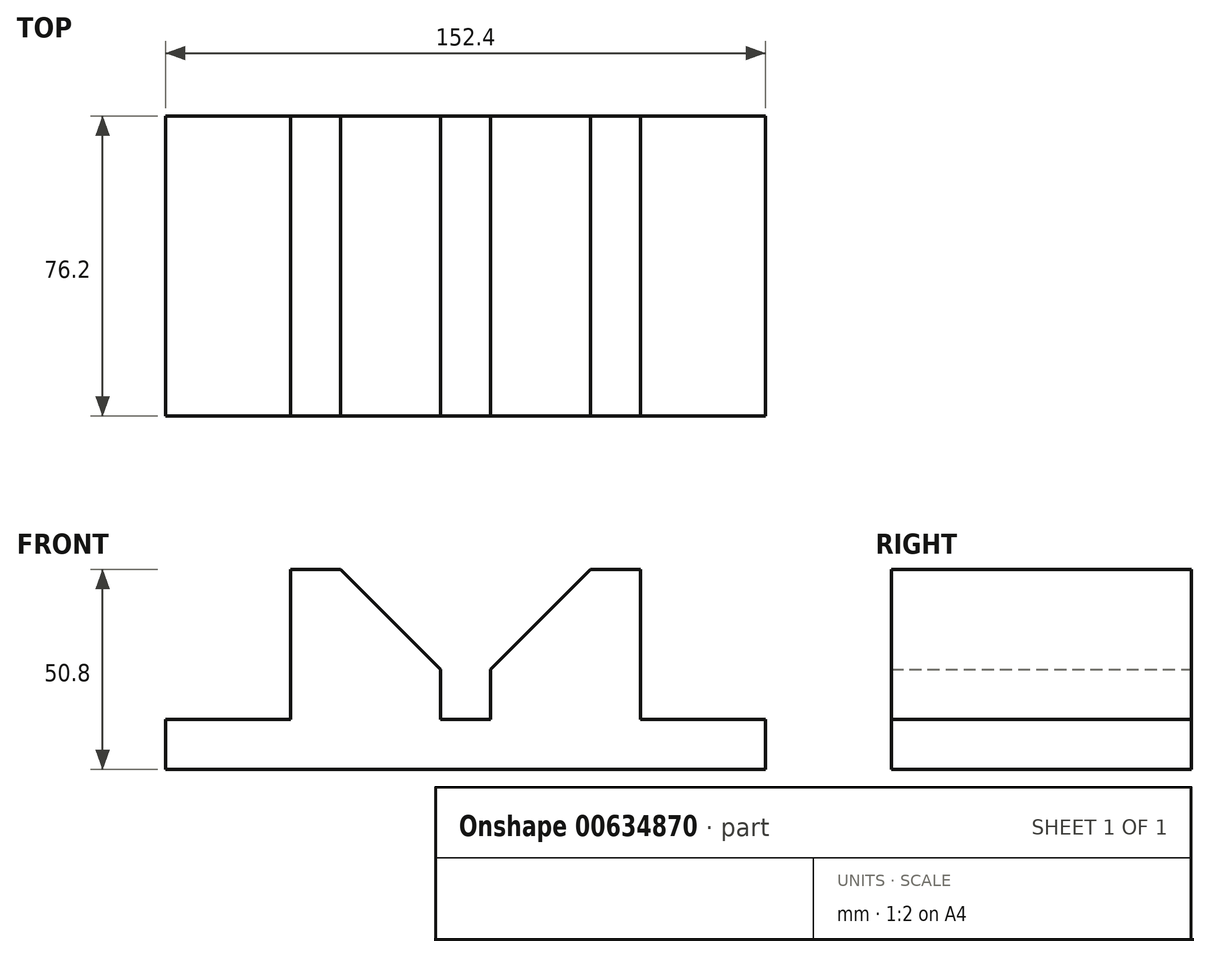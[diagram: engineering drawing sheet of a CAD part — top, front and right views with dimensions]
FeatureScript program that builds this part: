
annotation { "Feature Type Name" : "Feature", "Feature Type Description" : "" }
export const myFeature = defineFeature(function(context is Context, id is Id, definition is map)
    precondition{}
    {
        {
            var Q0;
            Q0=qCreatedBy(makeId("Front.planeOp"),FACE);
            var sketch = newSketch(context, id + "F0", { "sketchPlane" : qUnion([Q0])});
            skLineSegment(sketch, "E0", {"start": v(-82.34, -7.33) * mm, "end": v(-82.34, -20.03) * mm});
            skLineSegment(sketch, "E1", {"start": v(-82.34, -20.03) * mm, "end": v(70.06, -20.03) * mm});
            skLineSegment(sketch, "E2", {"start": v(70.06, -20.03) * mm, "end": v(70.06, -7.33) * mm});
            skLineSegment(sketch, "E3", {"start": v(70.06, -7.33) * mm, "end": v(38.3, -7.33) * mm});
            skLineSegment(sketch, "E4", {"start": v(38.3, -7.33) * mm, "end": v(38.3, 30.77) * mm});
            skLineSegment(sketch, "E5", {"start": v(38.3, 30.77) * mm, "end": v(25.6, 30.77) * mm});
            skLineSegment(sketch, "E6", {"start": v(25.6, 30.77) * mm, "end": v(0.2, 5.37) * mm});
            skLineSegment(sketch, "E7", {"start": v(0.2, 5.37) * mm, "end": v(0.2, -7.33) * mm});
            skLineSegment(sketch, "E8", {"start": v(0.2, -7.33) * mm, "end": v(-12.5, -7.33) * mm});
            skLineSegment(sketch, "E9", {"start": v(-12.5, -7.33) * mm, "end": v(-12.5, 5.37) * mm});
            skLineSegment(sketch, "E10", {"start": v(-12.5, 5.37) * mm, "end": v(-37.9, 30.77) * mm});
            skLineSegment(sketch, "E11", {"start": v(-37.9, 30.77) * mm, "end": v(-50.6, 30.77) * mm});
            skLineSegment(sketch, "E12", {"start": v(-50.6, 30.77) * mm, "end": v(-50.6, -7.33) * mm});
            skLineSegment(sketch, "E13", {"start": v(-50.6, -7.33) * mm, "end": v(-82.34, -7.33) * mm});
            skSolve(sketch);
        }
        {
            var Q0;
            Q0 = qSketchRegion(id + "F0", true);
            extrude(context, id + "F1", {"entities" : qUnion([Q0]), "depth" : 76.2 * mm, "offsetDistance" : 25.4 * mm});
        }
    });
